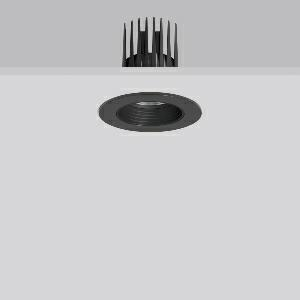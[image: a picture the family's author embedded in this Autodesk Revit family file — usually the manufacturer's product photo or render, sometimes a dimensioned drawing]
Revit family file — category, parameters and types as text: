
# Revit family: heledon_mini_e_901753_003_76_4fc3
name_source: partatom
category: Lighting Fixtures
units: mm (PartAtom-declared; Revit-internal decimal feet)

## family parameters
Cut with Voids When Loaded = No
Host = Face
Light Source = No
Part Type = Normal
Room Calculation Point = No
Round Connector Dimension = Use Diameter
Shared = No

## types (1)
- HELEDON mini E (1 x LED Modul 930, 2850 lm, 3000)
    Apparent Load = 29 VA
    Approval mark = CE
    CIE Flux Codes = 98 100 100 100 100
    Color Rendering = 90
    Color Temperature = 3000
    Default Elevation = 1800 mm
    Description = Series: HELEDON mini
Round recessed downlight. Housing: die-cast aluminium, powder-coated. Black plastic ring and recessed LED to prevent glare from the side. Optical assembly with lens made of plastic (polycarbonate) for the best homogeneous light distribution - can be changed without tools. Best colour rendering index Ra>90. Suitable for Recessed ceiling mounting. Installation without tools thanks to spring fastening system. Including separate LED converter with connecting cable 600 mm.High quality converter without flickering and stroboscopic effect. Through-wiring box (5 pole) available as accessory. The following accessories can be mounted without use of tools: interchangeable lenses, decorative glasses, honeycomb louvre, clear and frosted diffusers, white interchangeable plastic ring. 
Colour: deep black, matt (RAL 9005)
Diameter: 124 mm
Height: 3 mm
Cut-out diameter: 114 mm
Recess height: 170 mm
Luminaire: recess height: 120 mm
Lamp: LED
Socket: without socket
Colour temperature: 3000K
Colour rendering index (CRI): 92
System power: 29 W
Rated luminous flux: 2850 lm
Luminous efficiency: 98 lm/W
Control gear: Converter, dimmable, DALI
Protection class: II
Type of protection: IP 20
    Height = 0 mm  [stored 0 ft]
    Lamp = 1 x LED Modul 930
    Lamp Light Flux = 2850 lm
    Lamp count = 1
    Length = 124 mm  [stored 0.406824 ft]
    Lifetime = 50000 h
    Luminous efficacy = 98 lm/W
    Manufacturer = RZB
    ModVariant = No
    Model = 901753.003.76
    Mounting Place = Ceiling
    Mounting Type = Recessed
    Number of Poles = 1
    OnlyDefault = Yes
    Power Factor = 1
    Product Name = HELEDON mini E
    Product group = Recessed downlights
    ProductGroupID = 402
    Protection Class = Protection class II
    Protection Degree = IP 20
    RLX_Detail_Level = 1
    RLX_Emergency_Light_Flux = 0 lm
    RLX_Emergency_Type = 0
    RLX_Emergency_Type_DB = No
    RlxData = <blob elided: 125729 chars, md5=cd767f89>
    Socket = socket
    Standby Power = 0 W
    System Light Flux = 2850 lm
    System Power = 29 W
    Type Comments = Product without accessories
    Type Image = 901656.003.jpg
    URL = http://relux.com
    VarID = ---
    Voltage = 230 V
    Voltage Range = 220-240 V
    Weight = 0.00 kg
    Width = 0 mm  [stored 0 ft]

note: [stored X ft] marks values corroborated as IEEE doubles in the binary element streams (Revit-internal decimal feet)

## geometry (parser evidence)
native form markers: Blend x4, Sweep x10
no freeform markers — native parametric forms only
